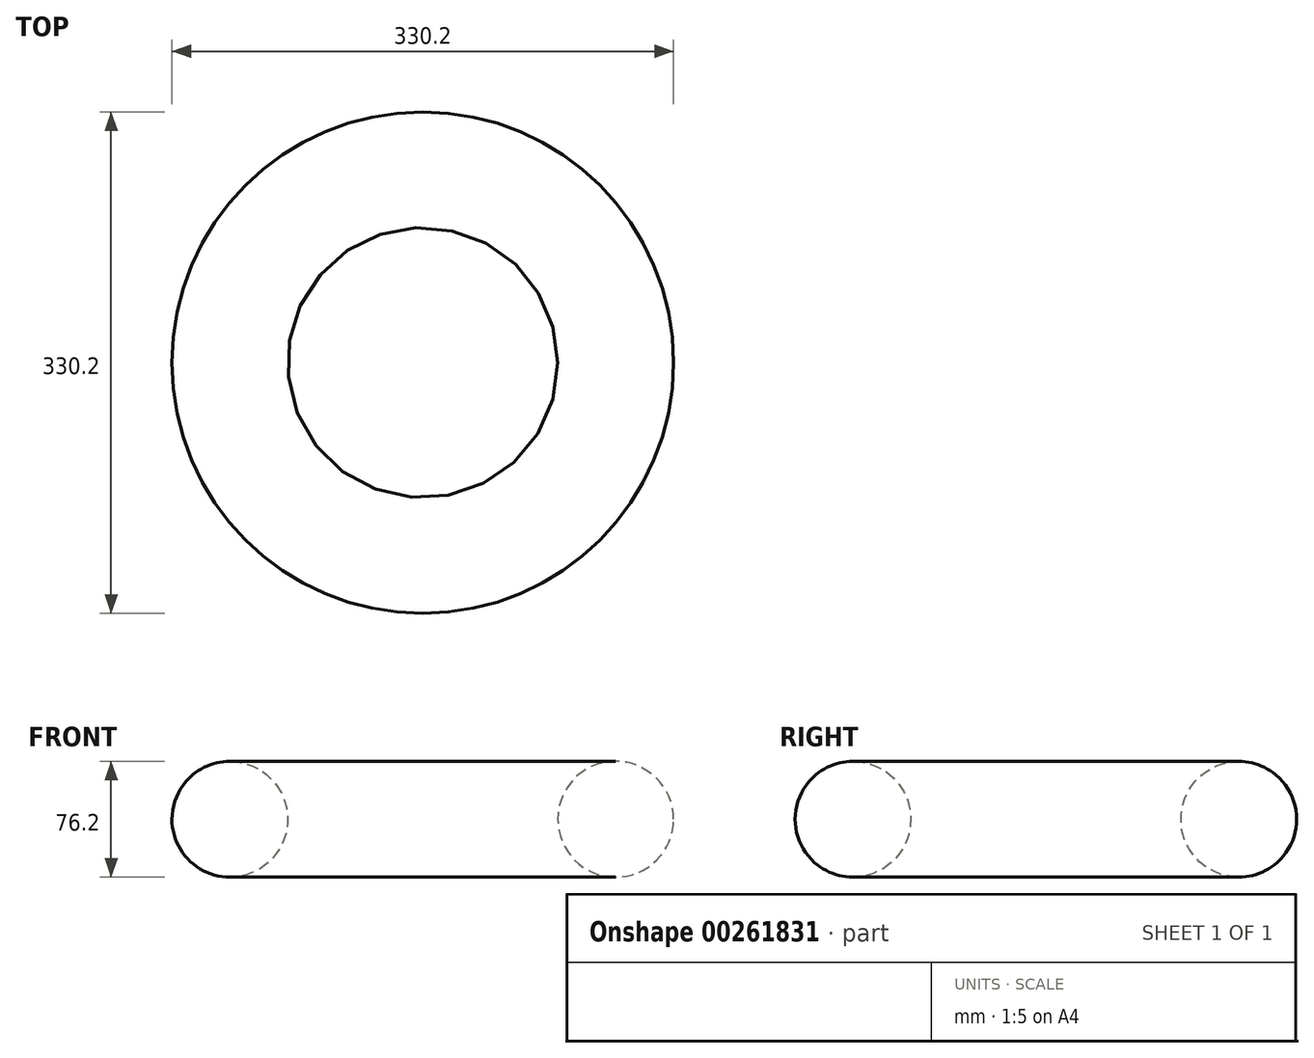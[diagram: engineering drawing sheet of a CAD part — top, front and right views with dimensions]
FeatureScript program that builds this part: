
annotation { "Feature Type Name" : "Feature", "Feature Type Description" : "" }
export const myFeature = defineFeature(function(context is Context, id is Id, definition is map)
    precondition{}
    {
        {
            var Q0;
            Q0=qCreatedBy(makeId("Front.planeOp"),FACE);
            var sketch = newSketch(context, id + "F0", { "sketchPlane" : qUnion([Q0])});
            skCircle(sketch, "E0", {"center": v(-127, 0.16) * mm, "radius": 38.1 * mm});
            skSolve(sketch);
        }
        {
            var Q0;
            Q0=qCreatedBy(makeId("Front.planeOp"),FACE);
            var sketch = newSketch(context, id + "F1", { "sketchPlane" : qUnion([Q0])});
            skLineSegment(sketch, "E1", {"start": v(0, 100.4) * mm, "end": v(0, -99.18) * mm, "construction": true});
            skSolve(sketch);
        }
        {
            var Q0;
            Q0=makeQuery(id+"F0.imprint","IMPRINT",FACE,{"disambiguationData":[TD([[makeQuery(id+"F0.imprint","IMPRINT",EDGE,{"derivedFrom":sQuery(id+"F0.wireOp",EDGE,"E0")}),1.0]])]});
            var Q1;
            Q1=sQuery(id+"F1.wireOp",EDGE,"E1");
            revolve(context, id + "F2", {"entities" : qUnion([Q0]), "axis" : qUnion([Q1]), "revolveType" : RevolveType.FULL});
        }
    });
